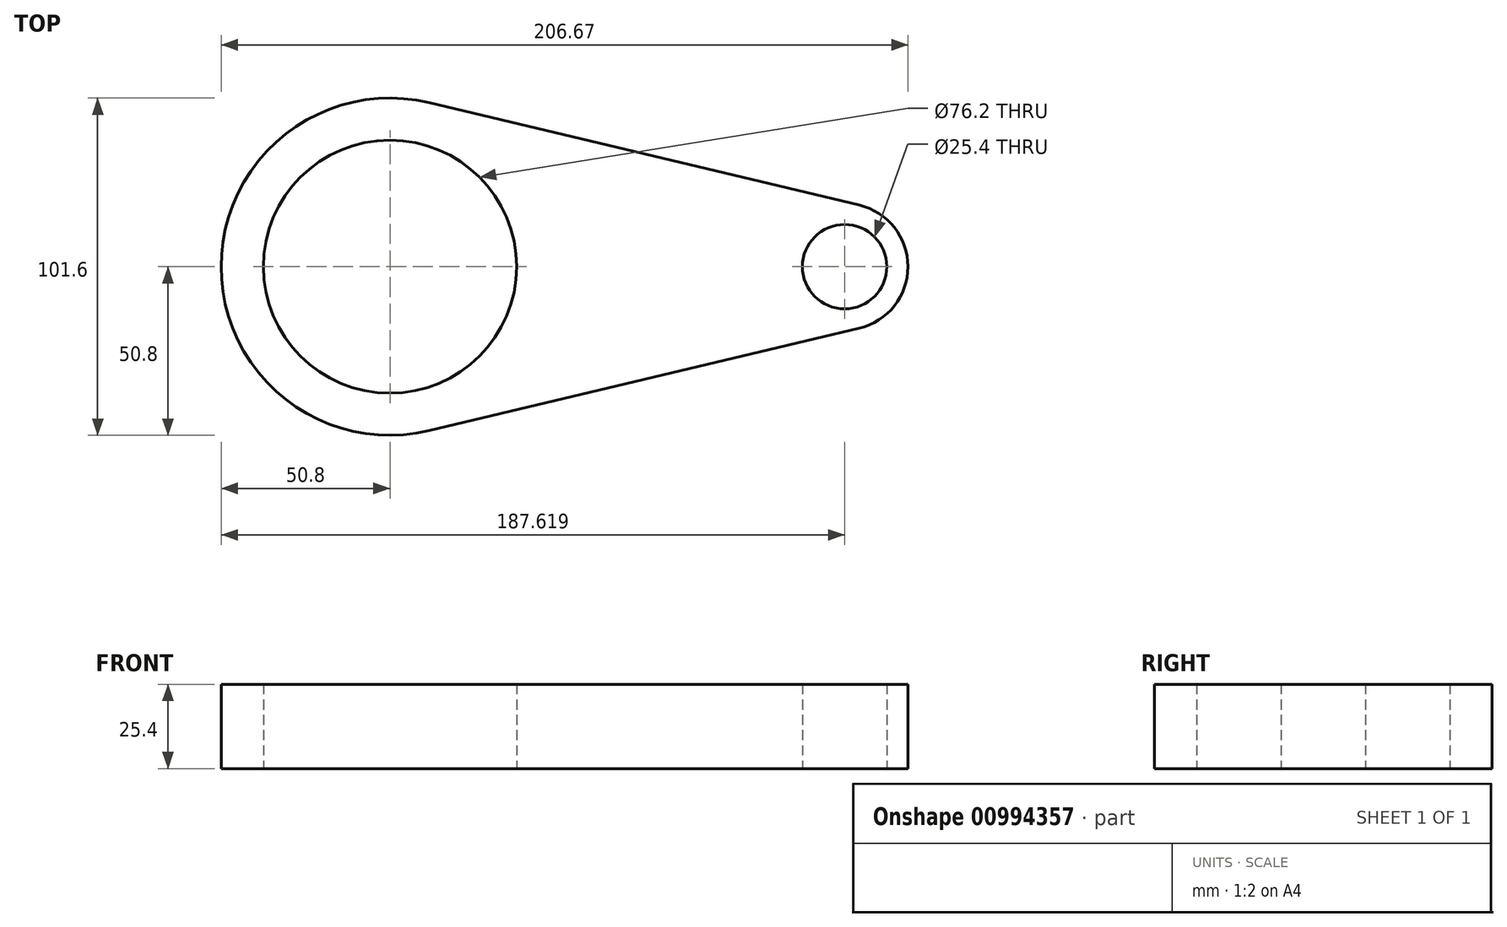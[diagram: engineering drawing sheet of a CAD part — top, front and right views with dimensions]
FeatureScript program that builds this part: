
annotation { "Feature Type Name" : "Feature", "Feature Type Description" : "" }
export const myFeature = defineFeature(function(context is Context, id is Id, definition is map)
    precondition{}
    {
        {
            var Q0;
            Q0=qCreatedBy(makeId("Top.planeOp"),FACE);
            var sketch = newSketch(context, id + "F0", { "sketchPlane" : qUnion([Q0])});
            skCircle(sketch, "E0", {"center": v(0, 0) * mm, "radius": 50.8 * mm});
            skCircle(sketch, "E1", {"center": v(136.82, 0) * mm, "radius": 19.05 * mm});
            skLineSegment(sketch, "E2", {"start": v(141.24, 18.53) * mm, "end": v(11.79, 49.41) * mm});
            skLineSegment(sketch, "E3", {"start": v(141.24, -18.53) * mm, "end": v(11.79, -49.41) * mm});
            skCircle(sketch, "E4", {"center": v(0, 0) * mm, "radius": 38.1 * mm});
            skCircle(sketch, "E5", {"center": v(136.82, 0) * mm, "radius": 12.7 * mm});
            skSolve(sketch);
        }
        {
            var Q0;
            Q0 = qSketchRegion(id + "F0", true);
            extrude(context, id + "F1", {"entities" : qUnion([Q0]), "depth" : 25.4 * mm, "offsetDistance" : 25.4 * mm});
        }
    });
